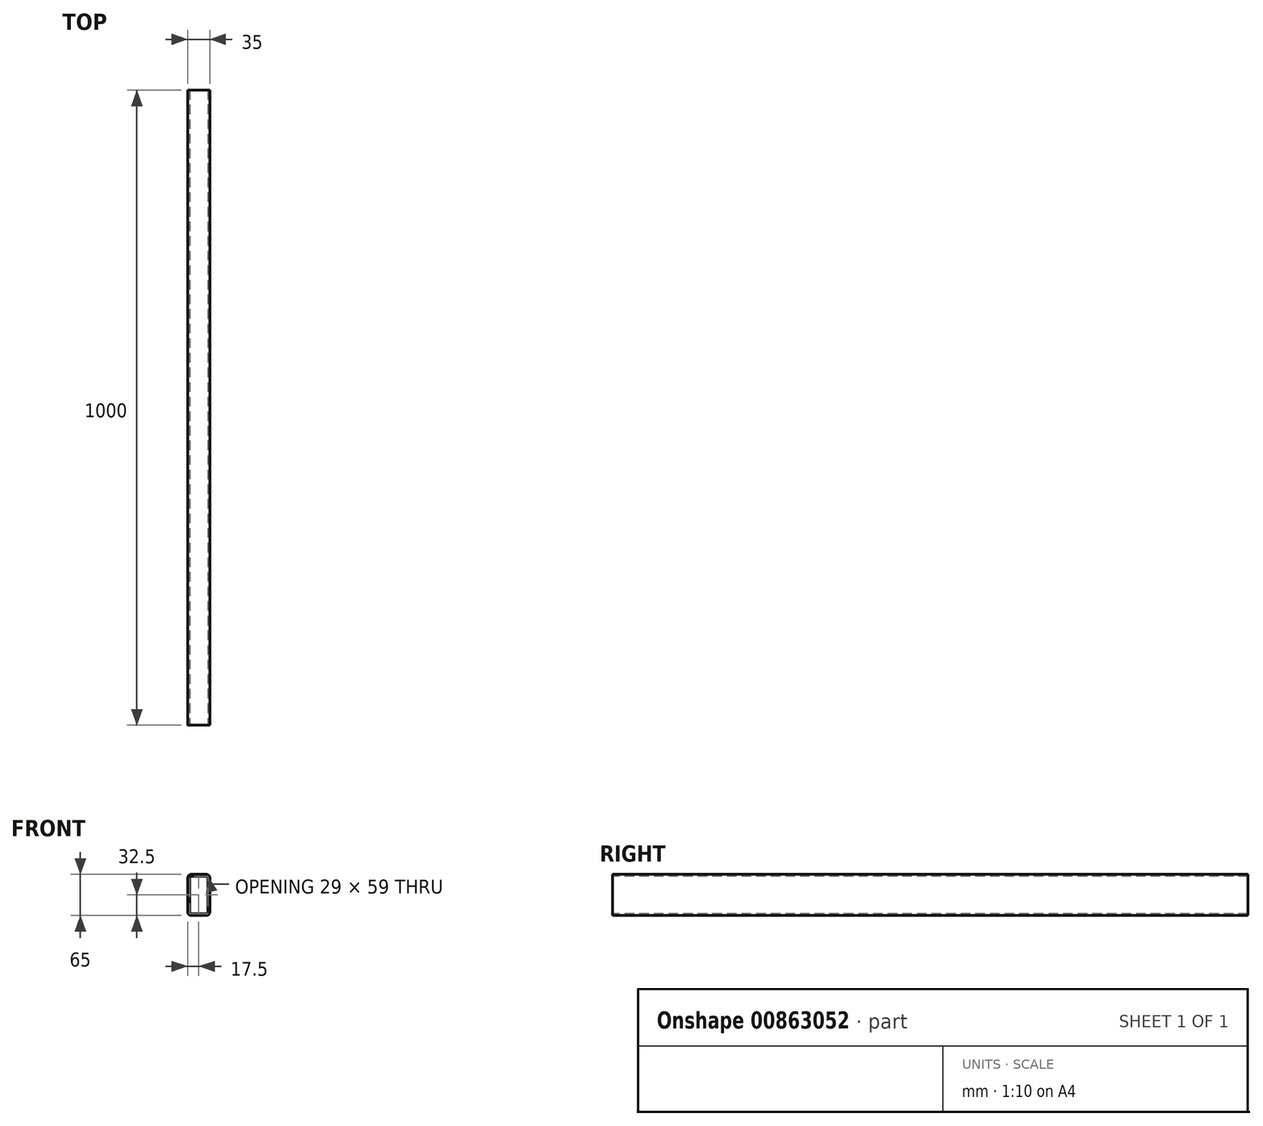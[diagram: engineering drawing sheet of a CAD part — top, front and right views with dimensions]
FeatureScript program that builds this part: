
annotation { "Feature Type Name" : "Feature", "Feature Type Description" : "" }
export const myFeature = defineFeature(function(context is Context, id is Id, definition is map)
    precondition{}
    {
        {
            var Q0;
            Q0=qCreatedBy(makeId("Front.planeOp"),FACE);
            var sketch = newSketch(context, id + "F0", { "sketchPlane" : qUnion([Q0])});
            skLineSegment(sketch, "E0.bottom", {"start": v(11.5, -32.5) * mm, "end": v(-11.5, -32.5) * mm});
            skLineSegment(sketch, "E0.top", {"start": v(11.5, 32.5) * mm, "end": v(-11.5, 32.5) * mm});
            skLineSegment(sketch, "E0.left", {"start": v(17.5, -26.5) * mm, "end": v(17.5, 26.5) * mm});
            skLineSegment(sketch, "E0.right", {"start": v(-17.5, -26.5) * mm, "end": v(-17.5, 26.5) * mm});
            skPoint(sketch, "E0.middle", {"position": v(0, 0) * mm});
            skPoint(sketch, "E1.visualSharp", {"position": v(-17.5, 32.5) * mm});
            skArc(sketch, "E1.filletArc", {"start": v(-11.5, 32.5) * mm, "mid": v(-15.74, 30.74) * mm, "end": v(-17.5, 26.5) * mm});
            skPoint(sketch, "E2.visualSharp", {"position": v(17.5, 32.5) * mm});
            skArc(sketch, "E2.filletArc", {"start": v(17.5, 26.5) * mm, "mid": v(15.74, 30.74) * mm, "end": v(11.5, 32.5) * mm});
            skPoint(sketch, "E3.visualSharp", {"position": v(17.5, -32.5) * mm});
            skArc(sketch, "E3.filletArc", {"start": v(11.5, -32.5) * mm, "mid": v(15.74, -30.74) * mm, "end": v(17.5, -26.5) * mm});
            skPoint(sketch, "E4.visualSharp", {"position": v(-17.5, -32.5) * mm});
            skArc(sketch, "E4.filletArc", {"start": v(-17.5, -26.5) * mm, "mid": v(-15.74, -30.74) * mm, "end": v(-11.5, -32.5) * mm});
            skArc(sketch, "E5.0", {"start": v(11.5, -29.5) * mm, "mid": v(13.62, -28.62) * mm, "end": v(14.5, -26.5) * mm});
            skLineSegment(sketch, "E5.1", {"start": v(11.5, -29.5) * mm, "end": v(-11.5, -29.5) * mm});
            skLineSegment(sketch, "E5.2", {"start": v(14.5, -26.5) * mm, "end": v(14.5, 26.5) * mm});
            skArc(sketch, "E5.3", {"start": v(-14.5, -26.5) * mm, "mid": v(-13.62, -28.62) * mm, "end": v(-11.5, -29.5) * mm});
            skArc(sketch, "E5.4", {"start": v(14.5, 26.5) * mm, "mid": v(13.62, 28.62) * mm, "end": v(11.5, 29.5) * mm});
            skLineSegment(sketch, "E5.5", {"start": v(11.5, 29.5) * mm, "end": v(-11.5, 29.5) * mm});
            skArc(sketch, "E5.6", {"start": v(-11.5, 29.5) * mm, "mid": v(-13.62, 28.62) * mm, "end": v(-14.5, 26.5) * mm});
            skLineSegment(sketch, "E5.7", {"start": v(-14.5, -26.5) * mm, "end": v(-14.5, 26.5) * mm});
            skSolve(sketch);
        }
        {
            var Q0;
            Q0=makeQuery(id+"F0.imprint","IMPRINT",FACE,{"disambiguationData":[TD([[makeQuery(id+"F0.imprint","IMPRINT",EDGE,{"derivedFrom":sQuery(id+"F0.wireOp",EDGE,"E0.bottom")}),-1.0]])]});
            extrude(context, id + "F1", {"entities" : qUnion([Q0]), "flatOperationType" : FlatOperationType.REMOVE, "oppositeDirection" : true, "depth" : 1000 * mm, "offsetDistance" : 25 * mm, "domain" : OperationDomain.MODEL});
        }
    });
